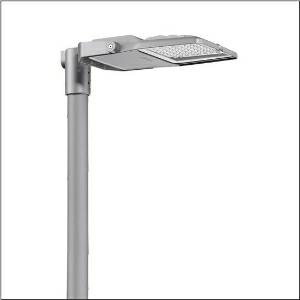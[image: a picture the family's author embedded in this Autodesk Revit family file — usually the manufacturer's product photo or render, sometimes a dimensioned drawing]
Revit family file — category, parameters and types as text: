
# Revit family: floodlight_fl_21_iq_mini___pl43_5xa7771d2a3a_a639
name_source: partatom
category: Lighting Fixtures
units: mm (PartAtom-declared; Revit-internal decimal feet)

## family parameters
Cut with Voids When Loaded = No
Host = Face
Light Source = No
Part Type = Normal
Room Calculation Point = No
Round Connector Dimension = Use Diameter
Shared = No

## types (1)
- --- (1 x LED, 18290 lm, 143 W, 3000K)
    Apparent Load = 143 VA
    CIE Flux Codes = 27 78 99 100 100
    Color Rendering = 70
    Color Temperature = 3000K
    Default Elevation = 1800 mm
    Description = Floodlight FL 21 iQ mini, floodlight, primary light control with lens, of PMMA, primary optical cover: protective disc, of toughened safety glass, transparent, light distribution: PL43, light emission: direct distribution, installation type: surface-mounted, LED, High Power LED, rated luminous flux: 18.290lm, luminous efficacy: 128lm/W, light colour: 730, colour temperature: 3000K, control gear: iQ Comfort/DALI, control: Auto-Match, Temp-Guard, Lumen-Switch, Night-Set, Smart-Wire, Light-Fading, Desk-Remote (wireless, voltage-free reading and setting of iQ features in the workshop via application-optimized NFC function/RFID function), optimised constant luminous flux control (CLO 2.0), with terminal, 6-pole, mains connection: 220..240V, AC, 50/60Hz, start of lifetime: 143W, end of service life: 152W, reduction: 61W, luminaire housing, of diecast aluminium, powder-coated, Siteco® metallic grey (DB 702S), corrosivity category C5 mid according to DIN EN ISO 12944, suitable for swimming pools, chlorine-resistant, sealing non-destructively replaceable, please order mast flange separately, mast bracket, of steel, galvanised, powder-coated, Siteco® metallic grey (DB 702S), protection rating (complete): IP66, insulation class (complete): insulation class II (safety insulation), certification: CE, ENEC, VDE, protection symbol: D, impact resistance: IK08, permissible operating ambient temperature: -40..+40°C, permissible operating ambient temperature for outdoor applications: -40..+50°C, standard: DIN EN 12944, LABS conformity tested according to VDMA 24364:2018-05, packaging unit: 1 piece

Light Distribution: PL43
    Height = 70 mm
    Lamp = 1 x LED
    Lamp Light Flux = 18290 lm
    Lamp Power = 143 W
    Lamp count = 1
    Length = 485 mm
    Luminous efficacy = 128 lm/W
    Manufacturer = Siteco
    ModVariant = No
    Model = 5XA7771D2A3A
    Number of Poles = 1
    OnlyDefault = Yes
    Power Factor = 1
    Product Name = Floodlight FL 21 iQ mini | PL43
    Product group = floodlight | pylon annexe
    ProductGroupID = 6200
    Protection Class = Protection class II
    Protection Degree = IP 66
    RLX_Detail_Level = 1
    RLX_Emergency_Light_Flux = 0 lm
    RLX_Emergency_Type = 0
    RLX_Emergency_Type_DB = No
    RlxData = <blob elided: 101513 chars, md5=0c0d24a7>
    Socket = socket
    Standby Power = 0 W
    System Light Flux = 18290 lm
    System Power = 143 W
    Type Comments = factory setting: luminous flux: 100 % | dim-lin: 254 | 730 mA
    Type Image = l_1007125.jpg
    URL = http://relux.com
    VarID = @adj_161866
    Voltage = 0 V
    Weight = 0.00 kg
    Width = 337 mm

## geometry (parser evidence)
native form markers: Blend x4, Sweep x12
no freeform markers — native parametric forms only
